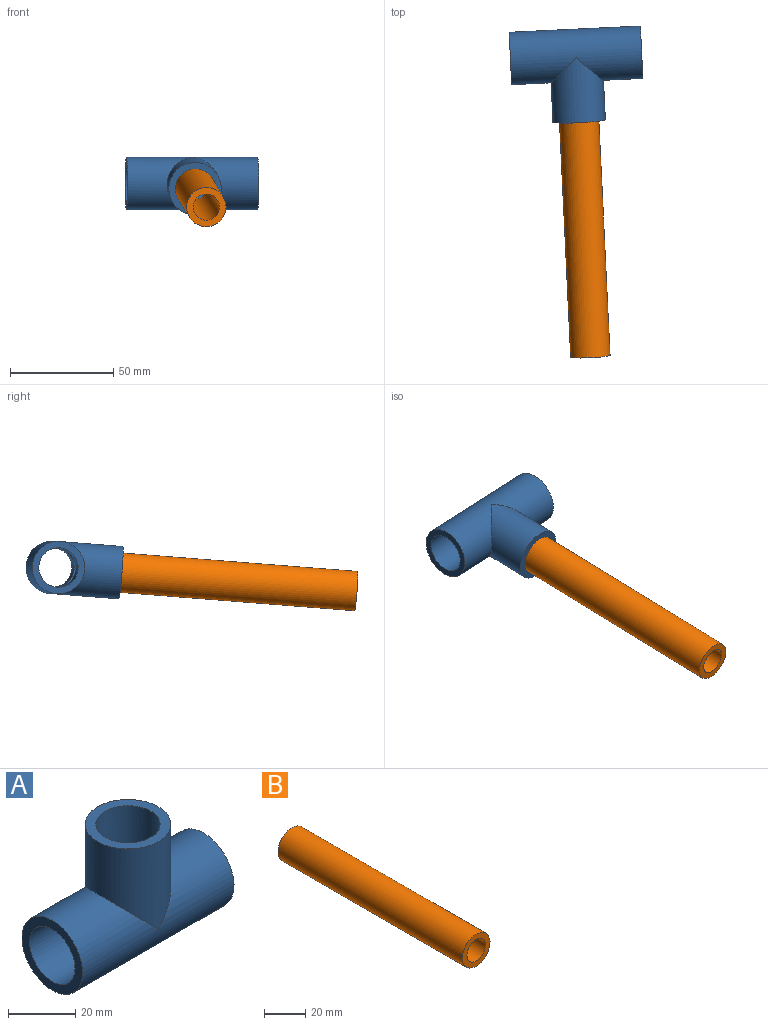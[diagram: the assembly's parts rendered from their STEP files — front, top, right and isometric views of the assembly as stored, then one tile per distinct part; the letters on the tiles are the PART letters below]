
ASSEMBLY  parts=2 mates=1
PART A: 7 faces, bbox 63.5x25.4x44.5 mm
  f0: plane 25.4x25.4mm, normal (1,0,0), area 221.7mm2, adj f3,f5
  f1: plane 25.4x25.4mm, normal (0,0,1), area 221.7mm2, adj f4,f6
  f2: plane 25.4x25.4mm, normal (-1,0,0), area 221.7mm2, adj f3,f5
  f3: cylinder r=12.7mm len=63.5mm, axis (1,0,0), area 4421.9mm2, adj f0,f2,f4
  f4: cylinder r=12.7mm len=31.75mm, axis (0,0,-1), area 1888.4mm2, adj f1,f3
  f5: cylinder r=9.53mm len=63.5mm, axis (1,0,0), area 3437.4mm2, adj f0,f2,f6
  f6: cylinder r=9.53mm len=31.75mm, axis (0,0,-1), area 1537.3mm2, adj f1,f5
PART B: 4 faces, bbox 19.1x127x19.1 mm
  f0: cylinder r=6.35mm len=127mm, axis (0,1,0), area 5067.1mm2, adj f2,f3
  f1: cylinder r=9.53mm len=127mm, axis (0,1,0), area 7600.6mm2, adj f2,f3
  f2: plane 19.05x19.05mm, normal (0,-1,0), area 158.3mm2, adj f0,f1
  f3: plane 19.05x19.05mm, normal (0,1,0), area 158.3mm2, adj f0,f1
PLACE A rot(axis=(-0.02,0.73,-0.68),178.1deg) t=(37.6,-139.34,18.88)mm
PLACE B rot(axis=(0.85,0.02,0.52),5.2deg) t=(7.45,-173.46,29.07)mm
MATE fastened A.f4 <-> B.f0  axis (0.05,-1,-0.08) through (8.05,-186.11,28.08)mm
